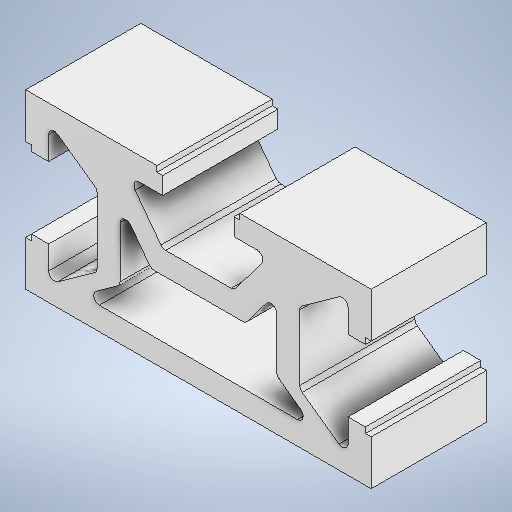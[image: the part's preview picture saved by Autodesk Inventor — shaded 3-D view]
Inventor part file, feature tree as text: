
AUTODESK INVENTOR PART (.ipt)
format: ipt  version: 2025.2 (Build 292293000, 293)  size: 331,776 bytes
history: native  units: mm
features: other x1, extrude x1, mirror x1, sketch x1
ambient origin geometry x8: Origin, YZ Plane, XZ Plane, XY Plane, X Axis, Y Axis, Z Axis, Center Point
bodies: Body1 (feature_tree)
feature tree (4):
  other  "Sólido1"
  extrude  "Extrusão1"  Depth=6.0mm
  mirror  "Espelhar1"
  sketch  "Esboço3"  dims[d33=15.0mm d34=6.0mm d35=30.0mm d36=2.0mm d37=6.2mm d38=2.0mm d39=3.0mm d40=6.2mm d41=2.0mm d43=3.0mm d44=2.0mm d45=2.0mm d46=2.0mm d47=0.5mm d52=0.5mm d61=10.0mm d62=0.0mm d27=0.5mm d28=0.872665mm d29=0.5mm d30=0.872665mm]
